# Revit family: Качели HARDWOOD «Канны» Арт 25367
name_source: partatom
category: Антураж
revit_build: Autodesk Revit 2018 (Build: 20180423_1000(x64)
units: mm (PartAtom-declared; Revit-internal decimal feet)

## family parameters
Всегда вертикально = Да
Источник визуального образа = Геометрия семейства
На основе рабочей плоскости = Нет
Общий = Нет
При загрузке вырезать с полостями = Нет
Точка расчета площади = Нет

## types (2) — shared parameters
URL = https://hobbyka.ru
Артикул товара = Арт. 25367
Высота = 2700 мм
Группа модели = Качели
Длина качели = 8300 мм
Длина площадки = 11300 мм
Изготовитель = ООО  «Хоббика»
Изображение типоразмера = Качели HARDWOOD «Канны».jpg
Материал изделия = Дерево
Описание = Качели HARDWOOD «Канны»
Производственный артикул = CWSw167.002
Цвет каркаса = Декрево
Цвет покрытия площадки = <По категории>
Ширина качели = 2060 мм
Ширина площадки = 8000 мм

## per-type parameters (varying)
| type | Модель с наклонными опорами | Модель с прямыми опорами |
| Модель с наклонными опорами | Да | Нет |
| Модель с прямыми опорами | Нет | Да |
